# Revit family: AB25G
name_source: partatom
category: Generic Models
revit_build: Autodesk Revit LT 2017 (Build: 20170118_1100(x64)
units: mm (PartAtom-declared; Revit-internal decimal feet)

## family parameters
Always vertical = No
Can host rebar = No
Cut with Voids When Loaded = No
Part Type = Normal
Room Calculation Point = No
Round Connector Dimension = Use Diameter
Shared = No
Work Plane-Based = Yes

## types (1)
- NBS Standard Parameters
    BIMObjectName = Metpro_metprolibrary_surfaceboxes_adaptablebox_plainsided
    Default Elevation = 1219 mm
    Description = AB24G - 300 X 300 X 150mm ( 12 X 12 X 6")  Adaptable Box - Plain
    DurationUnit = year
    Finish = Pre Galvanised Sheet Steel
    Keynote = Compliant to LU Standard 1-085
    ManufacturerName = Metpro Ltd
    ManufacturerURL = www.metpro.co.uk
    Material = Galvanised Steel Sheet
    ModelReference = AB25G
    NBSDescription = Surface Boxes
    NBSReference = 45-35-00/340
    NominalHeight = 100 mm  [stored 0.328084 ft]
    NominalLength = 300 mm
    NominalWidth = 300 mm
    ProductInformation = www.metpro.co.uk/pdf/ab25g.pdf
    Shape = Square
    Size = 300 X 300 X 150mm (12 X 12 X 6")
    Uniclass2 = Pr_65_52_01_86
    Version = 1
    WarrantyDurationUnit = 1 year
    Weight = 3.2437Kg

note: [stored X ft] marks values corroborated as IEEE doubles in the binary element streams (Revit-internal decimal feet)

## geometry (parser evidence)
native form markers: Sweep x2
no freeform markers — native parametric forms only
